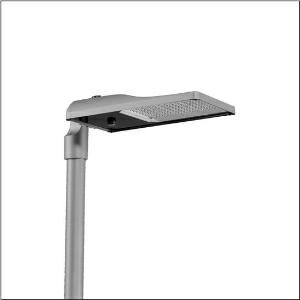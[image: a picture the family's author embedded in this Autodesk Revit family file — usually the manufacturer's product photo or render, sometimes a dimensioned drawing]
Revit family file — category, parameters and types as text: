
# Revit family: streetlight_sl_31_maxi___pl52_5xh8h31t08sa_1c4f
name_source: partatom
category: Lighting Fixtures
units: mm (PartAtom-declared; Revit-internal decimal feet)

## family parameters
Cut with Voids When Loaded = No
Host = Face
Light Source = No
Part Type = Normal
Room Calculation Point = No
Round Connector Dimension = Use Diameter
Shared = No

## types (1)
- --- (1 x LED, 27810 lm, 211.4 W, 3000K)
    Apparent Load = 211 VA
    CIE Flux Codes = 27 59 98 100 100
    Color Rendering = 70
    Color Temperature = 3000K
    Default Elevation = 1800 mm
    Description = Streetlight SL 31 maxi, mast luminaire, primary light control with lens, of PMMA, primary optical cover: cover, of toughened safety glass, transparent, light distribution: PL52, light emission: direct distribution, primary light characteristic: asymmetric, installation type: post-top, side-entry, LED, High Power LED, rated luminous flux: 27.810lm, luminous efficacy: 132lm/W, light colour: 730, colour temperature: 3000K, control: presetting dimming logarithmic, flexible luminous flux parameterisation, time-dependent luminous flux control, constant luminous flux control, power reduction, intelligent temperature release in ECG and LED module, overheat protection, with cable H07RN-F 2x 1.5mm², mains connection: 220..240V, AC, 50/60Hz, connection cable pre-assembled, cable length: 14,5m, start of lifetime: 211W, end of service life: 238W, reduction: 88W, luminaire housing, of diecast aluminium, powder-coated, Siteco® metallic grey (DB 702S), corrosivity category C5 high according to DIN EN ISO 12944, sealing non-destructively replaceable, multi-level sealing system, mast flange (76/60mm) included as standard, inclination: -15°..+20° (post-top) | -20°..+20° (side-entry), adjustable in 5° steps, no sealing on luminaire upper side, Smart Interface below and above, protection rating (complete): IP66, insulation class (complete): insulation class II (safety insulation), certification: CE, ENEC, ENEC+, VDE, UKCA, ZD4i, impact resistance: IK09, permissible operating ambient temperature for outdoor applications: -40..+50°C, standard-compliant lighting for roads and squares, packaging unit: 1 piece

Light Distribution: PL52
    Height = 79 mm
    Lamp = 1 x LED
    Lamp Light Flux = 27810 lm
    Lamp Power = 211.4 W
    Lamp count = 1
    Length = 657 mm
    Luminous efficacy = 132 lm/W
    Manufacturer = Siteco
    ModVariant = No
    Model = 5XH8H31T08SA
    Number of Poles = 1
    OnlyDefault = Yes
    Power Factor = 1
    Product Name = Streetlight SL 31 maxi | PL52
    Product group = mast luminaire | pylon top
    ProductGroupID = 6100
    Protection Class = Protection class II
    Protection Degree = IP 66
    RLX_Detail_Level = 1
    RLX_Emergency_Light_Flux = 0 lm
    RLX_Emergency_Type = 0
    RLX_Emergency_Type_DB = No
    RlxData = <blob elided: 56921 chars, md5=6bcb9df0>
    Socket = socket
    Standby Power = 0 W
    System Light Flux = 27810 lm
    System Power = 211 W
    Type Comments = factory setting: luminous flux: 100 % | dim-lin: 254 | 727 mA
    Type Image = l_1300303.jpg
    URL = http://relux.com
    VarID = @adj_002537
    Voltage = 0 V
    Weight = 0.00 kg
    Width = 362 mm

## geometry (parser evidence)
native form markers: Blend x4, Sweep x11
no freeform markers — native parametric forms only
